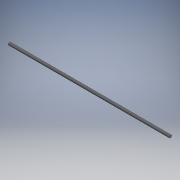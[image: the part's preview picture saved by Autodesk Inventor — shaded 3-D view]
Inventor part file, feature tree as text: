
AUTODESK INVENTOR PART (.ipt)
format: ipt  version: 2018 (Build 220112000, 112)  size: 95,744 bytes
history: native  units: in
note: dims shown in document units (in); Inventor stores cm internally (conversion verified against a paired STEP export)
features: revolve x1, thread x1, sketch x1
ambient origin geometry x8: Origin, YZ Plane, XZ Plane, XY Plane, X Axis, Y Axis, Z Axis, Center Point
bodies: Solid1 (feature_tree)
feature tree (3):
  revolve  "Revolution1"  [1 undecoded]
  thread  "Thread1"  [1 undecoded]
  sketch  "Sketch1"  dims[d0=0.1575in d1=16.9291in d2=90.0deg d3=0.3937in d4=0.0in]
note: 2 required parameter values undecoded (feature->parameter linkage not recoverable at this tier; creation-order binding heuristic only, values carry confidence <= 0.55)